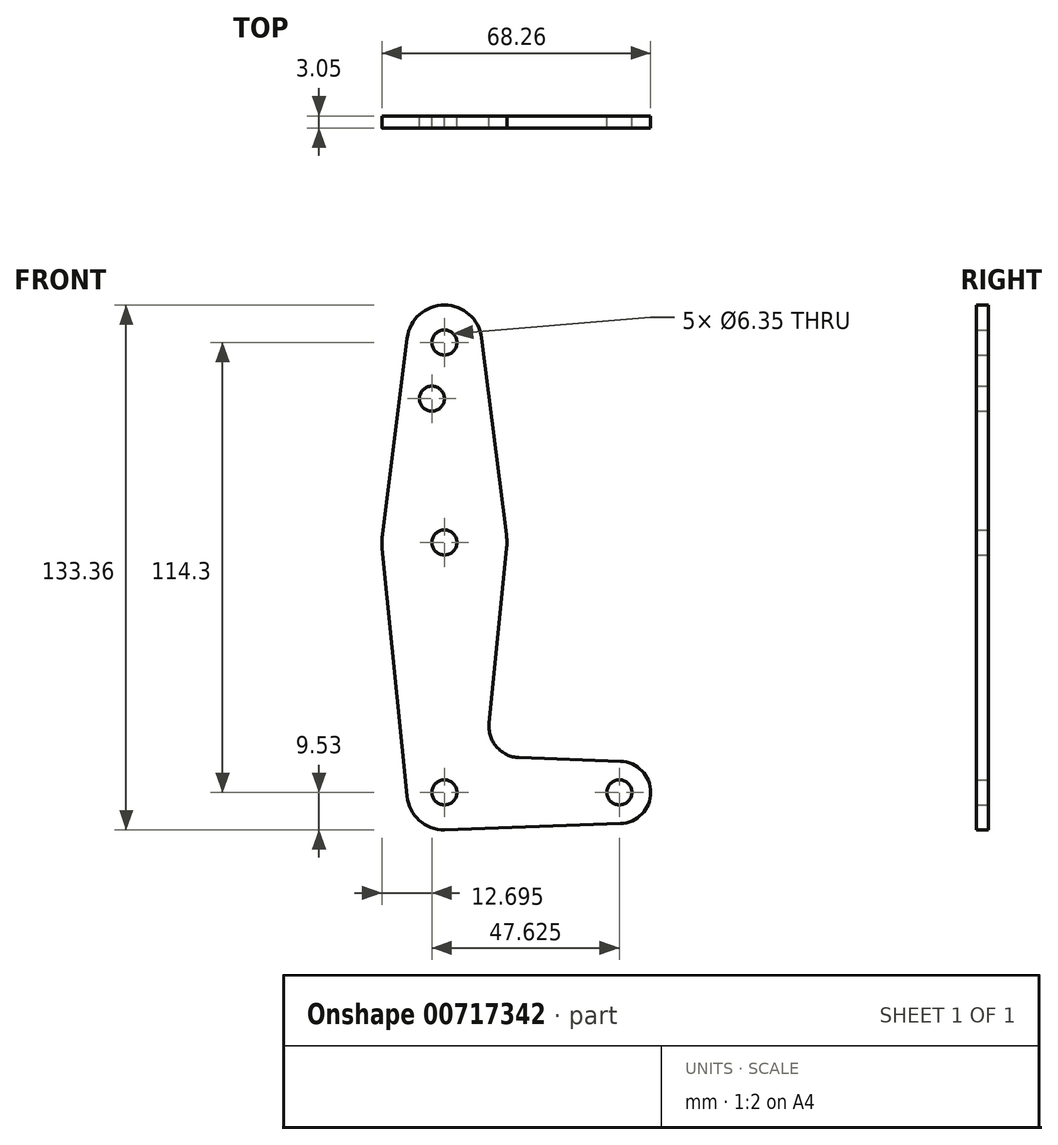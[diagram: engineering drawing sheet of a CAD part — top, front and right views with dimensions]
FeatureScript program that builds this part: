
annotation { "Feature Type Name" : "Feature", "Feature Type Description" : "" }
export const myFeature = defineFeature(function(context is Context, id is Id, definition is map)
    precondition{}
    {
        {
            var Q0;
            Q0=qCreatedBy(makeId("Front.planeOp"),FACE);
            var sketch = newSketch(context, id + "F0", { "sketchPlane" : qUnion([Q0])});
            skLineSegment(sketch, "E0", {"start": v(0, 0) * mm, "end": v(0, 114.3) * mm, "construction": true});
            skCircle(sketch, "E1", {"center": v(0, 114.3) * mm, "radius": 9.53 * mm});
            skCircle(sketch, "E2", {"center": v(0, 63.5) * mm, "radius": 15.88 * mm});
            skCircle(sketch, "E3", {"center": v(0, 0) * mm, "radius": 9.53 * mm});
            skLineSegment(sketch, "E4", {"start": v(0, 0) * mm, "end": v(44.45, 0) * mm, "construction": true});
            skCircle(sketch, "E5", {"center": v(44.45, 0) * mm, "radius": 7.94 * mm});
            skLineSegment(sketch, "E6", {"start": v(9.45, 115.5) * mm, "end": v(15.75, 65.48) * mm});
            skLineSegment(sketch, "E7", {"start": v(-9.45, 115.5) * mm, "end": v(-15.75, 65.48) * mm});
            skLineSegment(sketch, "E8", {"start": v(18.97, 8.85) * mm, "end": v(44.73, 7.93) * mm});
            skLineSegment(sketch, "E9", {"start": v(0, -9.52) * mm, "end": v(44.73, -7.93) * mm});
            skLineSegment(sketch, "E10", {"start": v(-15.8, 61.91) * mm, "end": v(-9.48, -0.95) * mm});
            skLineSegment(sketch, "E11", {"start": v(15.8, 61.91) * mm, "end": v(11.34, 17.59) * mm});
            skCircle(sketch, "E12", {"center": v(0, 114.3) * mm, "radius": 3.18 * mm});
            skCircle(sketch, "E13", {"center": v(-3.18, 100.03) * mm, "radius": 3.18 * mm});
            skCircle(sketch, "E14", {"center": v(0, 63.5) * mm, "radius": 3.18 * mm});
            skCircle(sketch, "E15", {"center": v(0, 0) * mm, "radius": 3.18 * mm});
            skCircle(sketch, "E16", {"center": v(44.45, 0) * mm, "radius": 3.18 * mm});
            skPoint(sketch, "E17.newPointA", {"position": v(9.57, 0) * mm});
            skArc(sketch, "E17.filletArc", {"start": v(11.34, 17.59) * mm, "mid": v(13.26, 11.57) * mm, "end": v(18.97, 8.85) * mm});
            skSolve(sketch);
        }
        {
            var Q0;
            {var subQ1=sQuery(id+"F0.wireOp",EDGE,"E6");Q0=makeQuery(id+"F0.imprint","IMPRINT",FACE,{"disambiguationData":[TD([[makeQuery(id+"F0.imprint","IMPRINT",EDGE,{"derivedFrom":subQ1}),-1.0]])]});}
            var Q1;
            Q1=makeQuery(id+"F0.imprint","IMPRINT",FACE,{"disambiguationData":[TD([[makeQuery(id+"F0.imprint","IMPRINT",EDGE,{"derivedFrom":sQuery(id+"F0.wireOp",EDGE,"E12")}),-1.0]])]});
            var Q2;
            Q2=makeQuery(id+"F0.imprint","IMPRINT",FACE,{"disambiguationData":[TD([[makeQuery(id+"F0.imprint","IMPRINT",EDGE,{"derivedFrom":sQuery(id+"F0.wireOp",EDGE,"E14")}),-1.0]])]});
            var Q3;
            {var subQ0=sQuery(id+"F0.wireOp",EDGE,"E8");Q3=makeQuery(id+"F0.imprint","IMPRINT",FACE,{"disambiguationData":[TD([[makeQuery(id+"F0.imprint","IMPRINT",EDGE,{"derivedFrom":subQ0}),-1.0]])]});}
            var Q4;
            Q4=makeQuery(id+"F0.imprint","IMPRINT",FACE,{"disambiguationData":[TD([[makeQuery(id+"F0.imprint","IMPRINT",EDGE,{"derivedFrom":sQuery(id+"F0.wireOp",EDGE,"E15")}),-1.0]])]});
            var Q5;
            Q5=makeQuery(id+"F0.imprint","IMPRINT",FACE,{"disambiguationData":[TD([[makeQuery(id+"F0.imprint","IMPRINT",EDGE,{"derivedFrom":sQuery(id+"F0.wireOp",EDGE,"E16")}),-1.0]])]});
            extrude(context, id + "F1", {"entities" : qUnion([Q0, Q1, Q2, Q3, Q4, Q5]), "depth" : 3.05 * mm, "offsetDistance" : 25.4 * mm});
        }
    });
